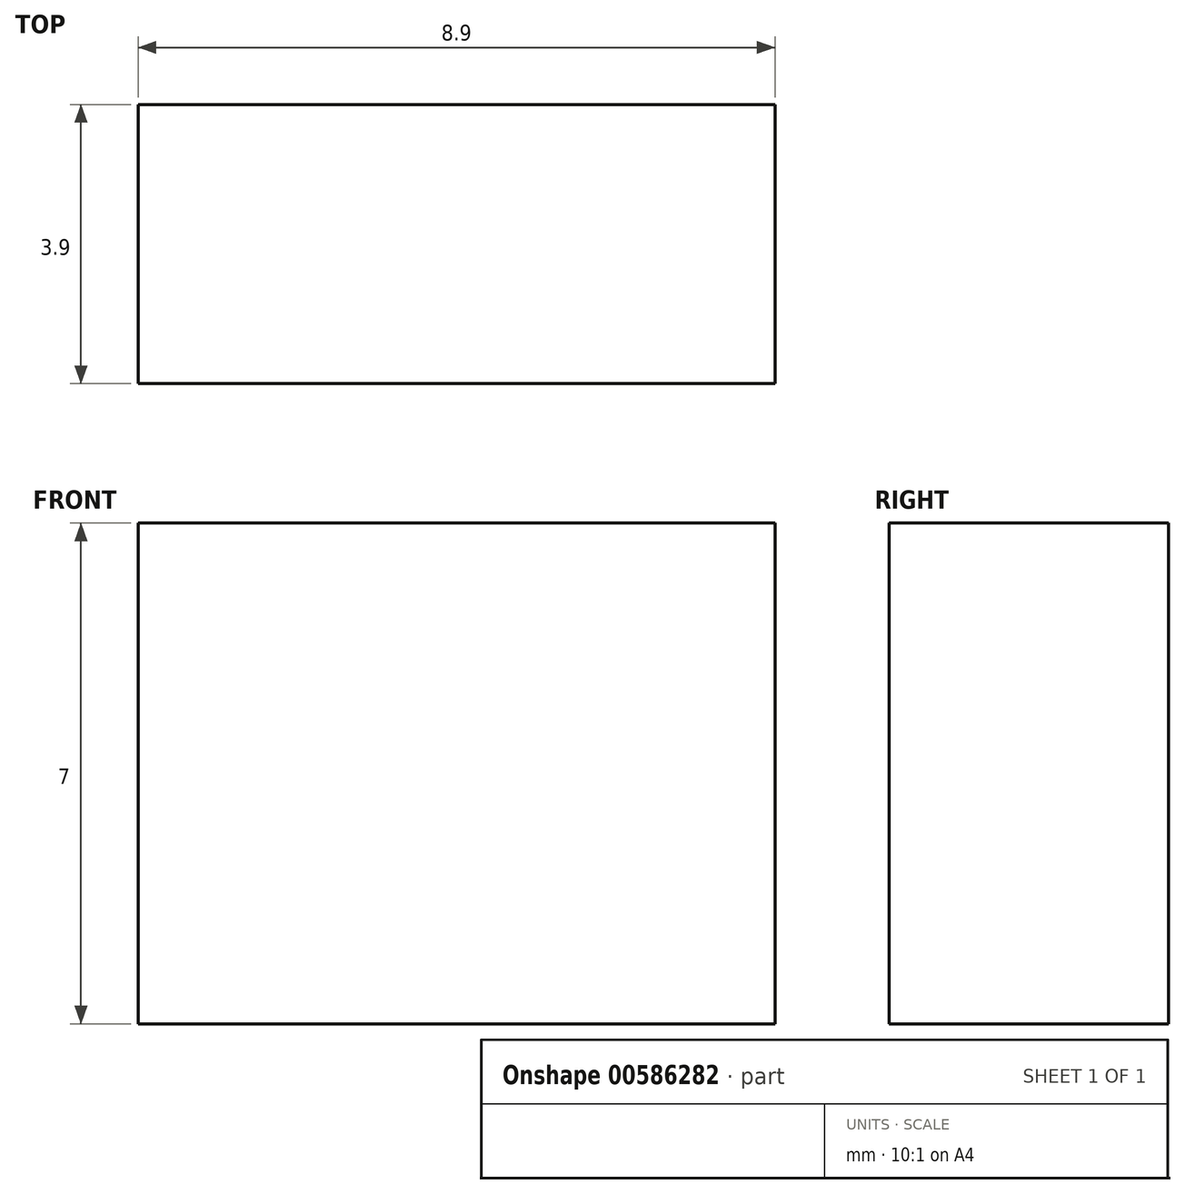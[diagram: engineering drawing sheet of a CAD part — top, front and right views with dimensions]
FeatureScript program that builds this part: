
annotation { "Feature Type Name" : "Feature", "Feature Type Description" : "" }
export const myFeature = defineFeature(function(context is Context, id is Id, definition is map)
    precondition{}
    {
        {
            var Q0;
            Q0=qCreatedBy(makeId("Top.planeOp"),FACE);
            var sketch = newSketch(context, id + "F0", { "sketchPlane" : qUnion([Q0])});
            skLineSegment(sketch, "E0.bottom", {"start": v(4.45, 1.95) * mm, "end": v(-4.45, 1.95) * mm});
            skLineSegment(sketch, "E0.top", {"start": v(4.45, -1.95) * mm, "end": v(-4.45, -1.95) * mm});
            skLineSegment(sketch, "E0.left", {"start": v(4.45, 1.95) * mm, "end": v(4.45, -1.95) * mm});
            skLineSegment(sketch, "E0.right", {"start": v(-4.45, 1.95) * mm, "end": v(-4.45, -1.95) * mm});
            skPoint(sketch, "E0.middle", {"position": v(0, 0) * mm});
            skSolve(sketch);
        }
        {
            var Q0;
            Q0 = qSketchRegion(id + "F0", true);
            extrude(context, id + "F1", {"entities" : qUnion([Q0]), "depth" : 7 * mm, "offsetDistance" : 25 * mm});
        }
    });
